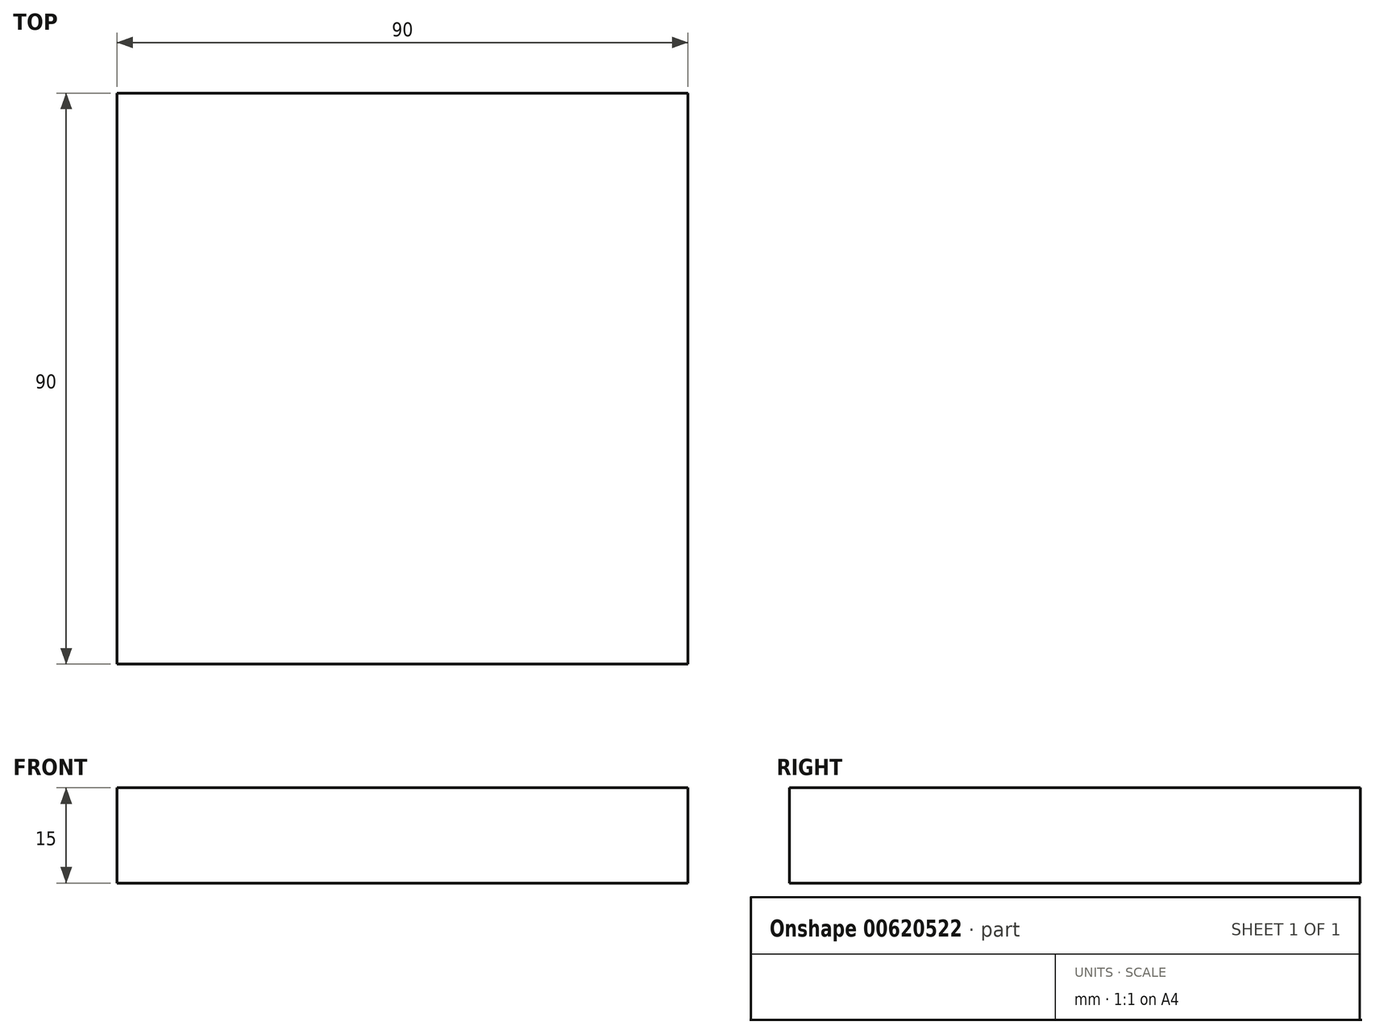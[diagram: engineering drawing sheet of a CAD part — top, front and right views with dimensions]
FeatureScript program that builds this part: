
annotation { "Feature Type Name" : "Feature", "Feature Type Description" : "" }
export const myFeature = defineFeature(function(context is Context, id is Id, definition is map)
    precondition{}
    {
        {
            var Q0;
            Q0=qCreatedBy(makeId("Top.planeOp"),FACE);
            var sketch = newSketch(context, id + "F0", { "sketchPlane" : qUnion([Q0])});
            skLineSegment(sketch, "E0.bottom", {"start": v(-53.95, 46.07) * mm, "end": v(36.05, 46.07) * mm});
            skLineSegment(sketch, "E0.top", {"start": v(-53.95, -43.93) * mm, "end": v(36.05, -43.93) * mm});
            skLineSegment(sketch, "E0.left", {"start": v(-53.95, 46.07) * mm, "end": v(-53.95, -43.93) * mm});
            skLineSegment(sketch, "E0.right", {"start": v(36.05, 46.07) * mm, "end": v(36.05, -43.93) * mm});
            skSolve(sketch);
        }
        {
            var Q0;
            Q0=makeQuery(id+"F0.imprint","IMPRINT",FACE,{"disambiguationData":[TD([[makeQuery(id+"F0.imprint","IMPRINT",EDGE,{"derivedFrom":sQuery(id+"F0.wireOp",EDGE,"E0.bottom")}),-1.0]])]});
            extrude(context, id + "F1", {"entities" : qUnion([Q0]), "depth" : 15 * mm, "offsetDistance" : 25.4 * mm});
        }
    });
